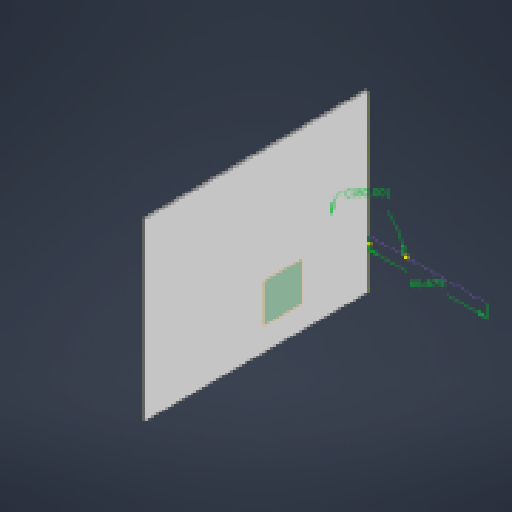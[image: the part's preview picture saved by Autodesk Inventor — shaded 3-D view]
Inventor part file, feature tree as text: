
AUTODESK INVENTOR PART (.ipt)
format: ipt  version: 2025 (Build 290162000, 162)  size: 120,832 bytes
history: native  units: mm
features: sketch x2, plane x1, extrude x1
ambient origin geometry x8: Origin, YZ Plane, XZ Plane, XY Plane, X Axis, Y Axis, Z Axis, Center Point
bodies: Solid1 (feature_tree)
feature tree (4):
  plane  "Work Plane1"
  extrude  "Extrusion2"  Depth=1.0mm
  sketch  "Sketch4"  dims[d9=180.0deg d2=0.5mm d3=0.872665mm]
  sketch  "Sketch2"  dims[d4=1.0mm d5=0.0mm d8=66.675mm]
